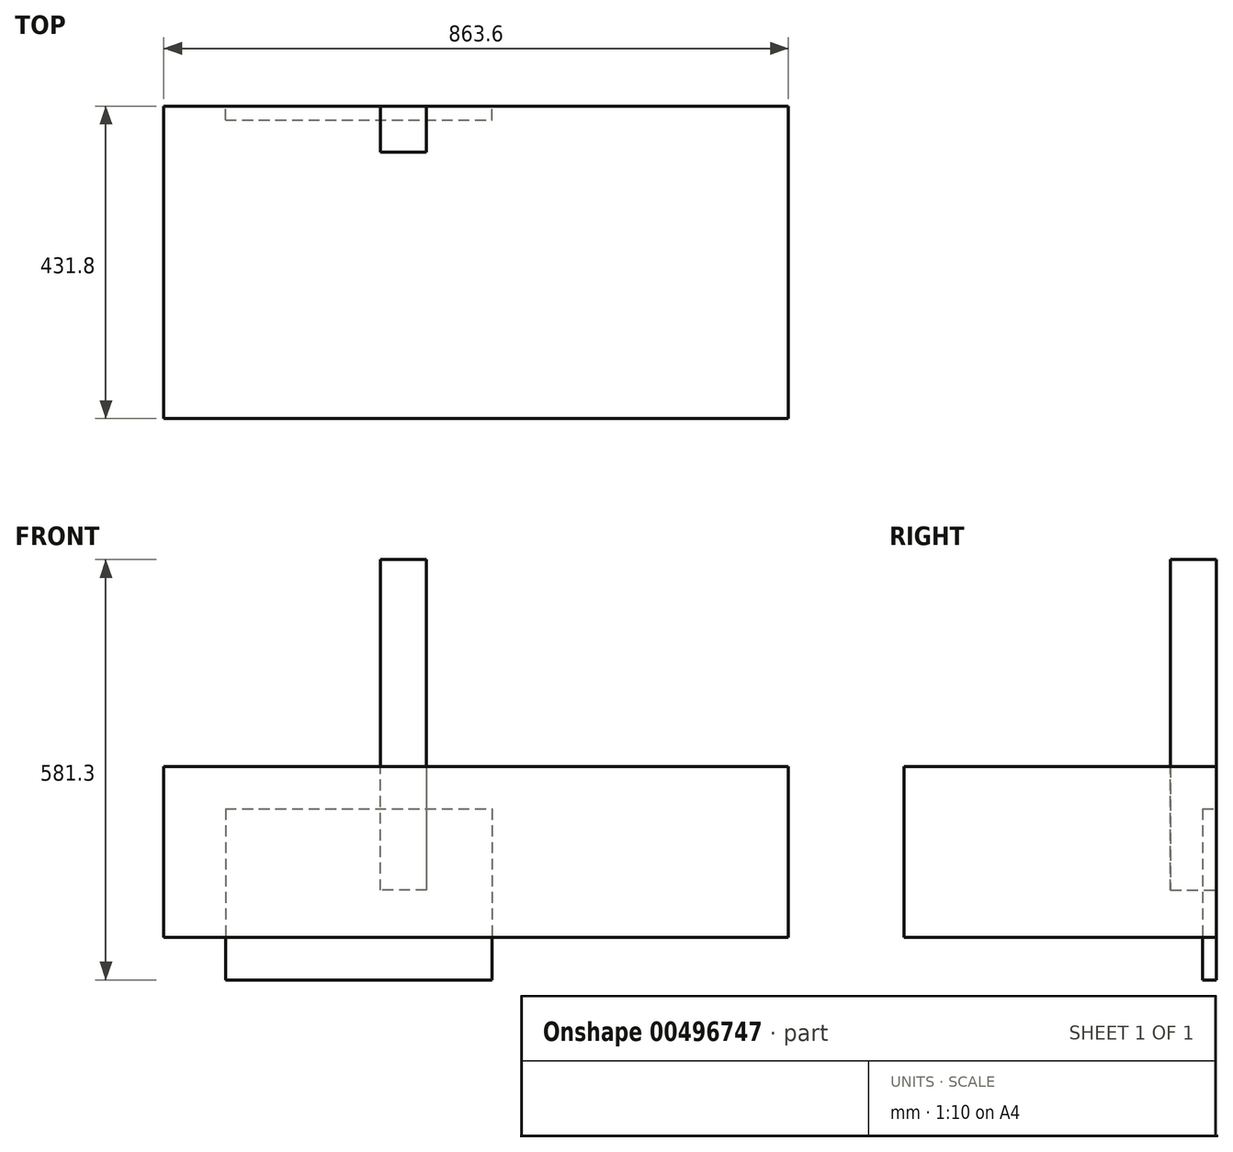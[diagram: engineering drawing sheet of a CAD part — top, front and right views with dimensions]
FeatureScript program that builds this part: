
annotation { "Feature Type Name" : "Feature", "Feature Type Description" : "" }
export const myFeature = defineFeature(function(context is Context, id is Id, definition is map)
    precondition{}
    {
        {
            var Q0;
            Q0=qCreatedBy(makeId("Front.planeOp"),FACE);
            var sketch = newSketch(context, id + "F0", { "sketchPlane" : qUnion([Q0])});
            skLineSegment(sketch, "E0", {"start": v(-18.1, 391.5) * mm, "end": v(45.4, 391.5) * mm});
            skLineSegment(sketch, "E1", {"start": v(45.4, 391.5) * mm, "end": v(45.4, -65.7) * mm});
            skLineSegment(sketch, "E2", {"start": v(45.4, -65.7) * mm, "end": v(-18.1, -65.7) * mm});
            skLineSegment(sketch, "E3", {"start": v(-18.1, -65.7) * mm, "end": v(-18.1, 391.5) * mm});
            skSolve(sketch);
        }
        {
            var Q0;
            Q0=makeQuery(id+"F0.imprint","IMPRINT",FACE,{"disambiguationData":[TD([[makeQuery(id+"F0.imprint","IMPRINT",EDGE,{"derivedFrom":sQuery(id+"F0.wireOp",EDGE,"E0")}),-1.0]])]});
            extrude(context, id + "F1", {"entities" : qUnion([Q0]), "depth" : 63.5 * mm});
        }
        {
            var Q0;
            Q0=qCreatedBy(makeId("Front.planeOp"),FACE);
            var sketch = newSketch(context, id + "F2", { "sketchPlane" : qUnion([Q0])});
            skLineSegment(sketch, "E4.bottom", {"start": v(-317.91, -131.25) * mm, "end": v(545.69, -131.25) * mm});
            skLineSegment(sketch, "E4.top", {"start": v(-317.91, 105.29) * mm, "end": v(545.69, 105.29) * mm});
            skLineSegment(sketch, "E4.left", {"start": v(-317.91, -131.25) * mm, "end": v(-317.91, 105.29) * mm});
            skLineSegment(sketch, "E4.right", {"start": v(545.69, -131.25) * mm, "end": v(545.69, 105.29) * mm});
            skSolve(sketch);
        }
        {
            var Q0;
            Q0=makeQuery(id+"F2.imprint","IMPRINT",FACE,{"disambiguationData":[TD([[makeQuery(id+"F2.imprint","IMPRINT",EDGE,{"derivedFrom":sQuery(id+"F2.wireOp",EDGE,"E4.bottom")}),1.0]])]});
            extrude(context, id + "F3", {"entities" : qUnion([Q0]), "depth" : 431.8 * mm});
        }
        {
            var Q0;
            Q0=makeQuery(id+"F2.imprint","IMPRINT",FACE,{"disambiguationData":[TD([[makeQuery(id+"F2.imprint","IMPRINT",EDGE,{"derivedFrom":sQuery(id+"F2.wireOp",EDGE,"E4.bottom")}),1.0]])]});
            var sketch = newSketch(context, id + "F4", { "sketchPlane" : qUnion([Q0])});
            skLineSegment(sketch, "E5.bottom", {"start": v(-232.53, 46.74) * mm, "end": v(135.77, 46.74) * mm});
            skLineSegment(sketch, "E5.top", {"start": v(-232.53, -189.8) * mm, "end": v(135.77, -189.8) * mm});
            skLineSegment(sketch, "E5.left", {"start": v(-232.53, 46.74) * mm, "end": v(-232.53, -189.8) * mm});
            skLineSegment(sketch, "E5.right", {"start": v(135.77, 46.74) * mm, "end": v(135.77, -189.8) * mm});
            skSolve(sketch);
        }
        {
            var Q0;
            Q0 = qSketchRegion(id + "F4", true);
            extrude(context, id + "F5", {"entities" : qUnion([Q0]), "depth" : 19.05 * mm});
        }
    });
